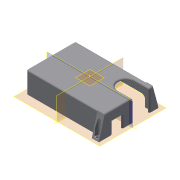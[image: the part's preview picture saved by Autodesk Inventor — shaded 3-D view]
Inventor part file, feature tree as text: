
AUTODESK INVENTOR PART (.ipt)
format: ipt  version: 2015 SP2 (Build 190223200, 223)  size: 244,224 bytes
history: native  units: mm
features: extrude x9, sketch x9, mirror x2, fillet x2, projected_geometry x2, other x1, plane x1
ambient origin geometry x8: Origin, YZ Plane, XZ Plane, XY Plane, X Axis, Y Axis, Z Axis, Center Point
bodies: Body1 (feature_tree)
feature tree (26):
  other  "Sólido1"
  plane  "Plano de trabajo1"
  extrude  "Extrusión1"  Depth=30.0mm
  extrude  "Extrusión2"  Depth=2.0mm TaperAngle=0.0deg
  extrude  "Extrusión3"  Depth=28.0mm TaperAngle=0.0deg
  extrude  "Extrusión4"  Depth=10.0mm TaperAngle=0.0deg
  extrude  "Extrusión6"  Depth=14.0mm
  mirror  "Simetría1"
  extrude  "Extrusión7"  Depth=10.0mm TaperAngle=0.0deg
  fillet  "Empalme2"  Radius=20.0mm
  sketch  "Boceto8"  dims[d22=12.0mm d23=6.0mm d24=10.0mm d25=0.0mm]
  extrude  "Extrusión9"  Depth=10.0mm
  fillet  "Empalme3"  Radius=10.0mm
  extrude  "Extrusión10"  Depth=14.148mm
  extrude  "Extrusión11"  Depth=28.0mm
  mirror  "Simetría3"
  sketch  "Boceto1"  dims[d0=30.0mm d1=110.0mm]
  sketch  "Boceto2"  dims[d2=69.0mm d3=2.0mm d4=0.0mm]
  sketch  "Boceto3"  dims[d5=2.0mm d6=28.0mm d7=0.0mm]
  sketch  "Boceto4"  dims[d8=18.31374mm d9=10.0mm d10=0.0mm]
  sketch  "Boceto6"  dims[d11=16.0mm d12=14.0mm]
  sketch  "Boceto7"  dims[d13=44.0mm d14=10.0mm d15=0.0mm d21=20.0mm]
  sketch  "Boceto9"  dims[d26=42.007mm d27=14.148mm]
  projected_geometry  "Contorno proyectado1"
  sketch  "Boceto10"  dims[d28=50.0mm d29=5.0mm d30=15.0mm d32=4.0mm d33=10.0mm d34=0.0mm d36=2.0mm d42=5.0mm d43=5.0mm d44=6.0mm d56=24.0mm d57=55.0mm d58=10.0mm d59=0.6mm d60=0.0mm d61=1.0mm d62=6.235mm d63=28.0mm d64=0.0mm d65=3.5mm d66=28.0mm d67=0.0mm]
  projected_geometry  "Contorno proyectado2"
